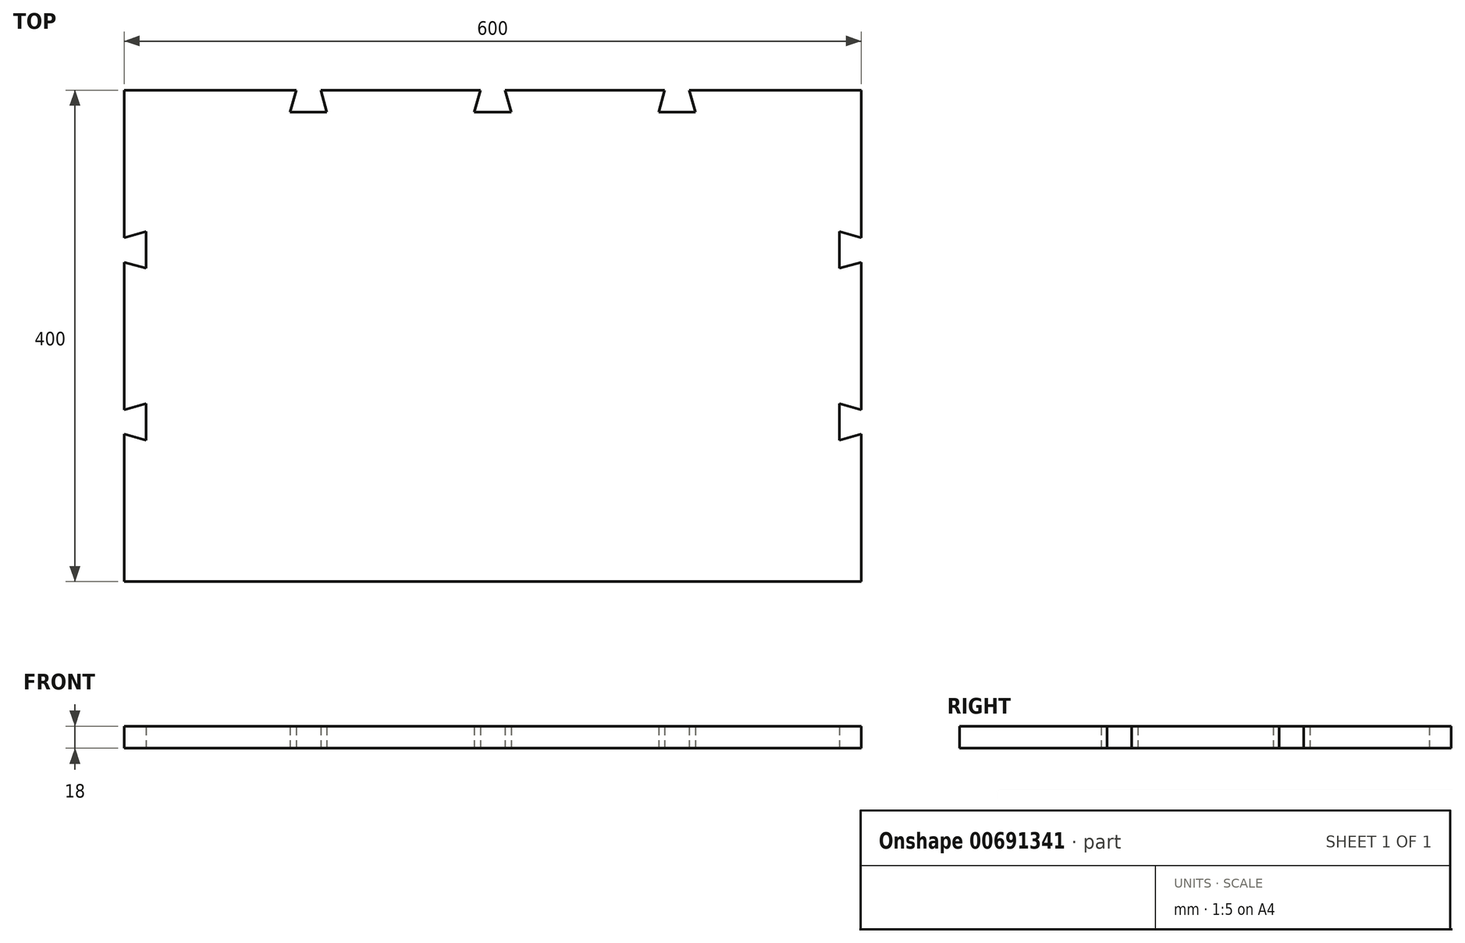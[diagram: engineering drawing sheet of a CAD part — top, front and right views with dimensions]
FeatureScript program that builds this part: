
annotation { "Feature Type Name" : "Feature", "Feature Type Description" : "" }
export const myFeature = defineFeature(function(context is Context, id is Id, definition is map)
    precondition{}
    {
        {
            var Q0;
            Q0=qCreatedBy(makeId("Right.planeOp"),FACE);
            var sketch = newSketch(context, id + "F0", { "sketchPlane" : qUnion([Q0])});
            skLineSegment(sketch, "E0", {"start": v(0, 0) * mm, "end": v(0, 18) * mm});
            skLineSegment(sketch, "E1", {"start": v(0, 18) * mm, "end": v(400, 18) * mm});
            skLineSegment(sketch, "E2", {"start": v(400, 18) * mm, "end": v(400, 0) * mm});
            skLineSegment(sketch, "E3", {"start": v(400, 0) * mm, "end": v(0, 0) * mm});
            skSolve(sketch);
        }
        {
            var Q0;
            Q0=makeQuery(id+"F0.imprint","IMPRINT",FACE,{"disambiguationData":[TD([[makeQuery(id+"F0.imprint","IMPRINT",EDGE,{"derivedFrom":sQuery(id+"F0.wireOp",EDGE,"E0")}),-1.0]])]});
            extrude(context, id + "F1", {"entities" : qUnion([Q0]), "oppositeDirection" : true, "depth" : 600 * mm, "offsetDistance" : 25 * mm});
        }
        {
            var Q0;
            Q0=qCreatedBy(makeId("Top.planeOp"),FACE);
            var sketch = newSketch(context, id + "F2", { "sketchPlane" : qUnion([Q0])});
            skLineSegment(sketch, "E4", {"start": v(-300, -47.28) * mm, "end": v(-300, 479.56) * mm, "construction": true});
            skLineSegment(sketch, "E5", {"start": v(-652.6, 200) * mm, "end": v(61.07, 200) * mm, "construction": true});
            skLineSegment(sketch, "E6", {"start": v(-310, 400) * mm, "end": v(-315, 382) * mm});
            skLineSegment(sketch, "E7", {"start": v(-315, 382) * mm, "end": v(-300, 382) * mm});
            skLineSegment(sketch, "E8", {"start": v(-310, 400) * mm, "end": v(-300, 400) * mm});
            skLineSegment(sketch, "E9.MirrorCS", {"start": v(-290, 400) * mm, "end": v(-285, 382) * mm});
            skLineSegment(sketch, "E10", {"start": v(-300, 382) * mm, "end": v(-285, 382) * mm});
            skLineSegment(sketch, "E11", {"start": v(-300, 400) * mm, "end": v(-290, 400) * mm});
            skLineSegment(sketch, "E12.1.0.0", {"start": v(-160, 400) * mm, "end": v(-165, 382) * mm});
            skLineSegment(sketch, "E12.1.0.1", {"start": v(-160, 400) * mm, "end": v(-150, 400) * mm});
            skLineSegment(sketch, "E12.1.0.2", {"start": v(-150, 400) * mm, "end": v(-140, 400) * mm});
            skLineSegment(sketch, "E12.1.0.3", {"start": v(-140, 400) * mm, "end": v(-135, 382) * mm});
            skLineSegment(sketch, "E13.1.0.0", {"start": v(-460, 400) * mm, "end": v(-465, 382) * mm});
            skLineSegment(sketch, "E13.1.0.1", {"start": v(-460, 400) * mm, "end": v(-450, 400) * mm});
            skLineSegment(sketch, "E13.1.0.2", {"start": v(-450, 400) * mm, "end": v(-440, 400) * mm});
            skLineSegment(sketch, "E13.1.0.3", {"start": v(-440, 400) * mm, "end": v(-435, 382) * mm});
            skLineSegment(sketch, "E14", {"start": v(-135, 382) * mm, "end": v(-165, 382) * mm});
            skLineSegment(sketch, "E15", {"start": v(-435, 382) * mm, "end": v(-465, 382) * mm});
            skLineSegment(sketch, "E16", {"start": v(-600, 260) * mm, "end": v(-600, 270) * mm, "construction": true});
            skLineSegment(sketch, "E17", {"start": v(-600, 270) * mm, "end": v(-582, 270) * mm, "construction": true});
            skLineSegment(sketch, "E18", {"start": v(-600, 270) * mm, "end": v(-600, 280) * mm});
            skLineSegment(sketch, "E19", {"start": v(-600, 280) * mm, "end": v(-582, 285) * mm});
            skLineSegment(sketch, "E20", {"start": v(-582, 285) * mm, "end": v(-582, 270) * mm});
            skLineSegment(sketch, "E21.MirrorCS", {"start": v(-600, 270) * mm, "end": v(-600, 260) * mm});
            skLineSegment(sketch, "E22.MirrorCS", {"start": v(-600, 260) * mm, "end": v(-582, 255) * mm});
            skLineSegment(sketch, "E23.MirrorCS", {"start": v(-582, 255) * mm, "end": v(-582, 270) * mm});
            skLineSegment(sketch, "E24.MirrorCS", {"start": v(-600, 140) * mm, "end": v(-582, 145) * mm});
            skLineSegment(sketch, "E25.MirrorCS", {"start": v(-582, 145) * mm, "end": v(-582, 130) * mm});
            skLineSegment(sketch, "E26.MirrorCS", {"start": v(-582, 115) * mm, "end": v(-582, 130) * mm});
            skLineSegment(sketch, "E27.MirrorCS", {"start": v(-600, 120) * mm, "end": v(-582, 115) * mm});
            skLineSegment(sketch, "E28.MirrorCS", {"start": v(-600, 130) * mm, "end": v(-600, 120) * mm});
            skLineSegment(sketch, "E29.MirrorCS", {"start": v(0, 280) * mm, "end": v(-18, 285) * mm});
            skLineSegment(sketch, "E30.MirrorCS", {"start": v(-18, 285) * mm, "end": v(-18, 270) * mm});
            skLineSegment(sketch, "E31.MirrorCS", {"start": v(0, 270) * mm, "end": v(0, 280) * mm});
            skLineSegment(sketch, "E32.MirrorCS", {"start": v(0, 260) * mm, "end": v(-18, 255) * mm});
            skLineSegment(sketch, "E33.MirrorCS", {"start": v(-18, 255) * mm, "end": v(-18, 270) * mm});
            skLineSegment(sketch, "E34.MirrorCS", {"start": v(0, 270) * mm, "end": v(0, 260) * mm});
            skLineSegment(sketch, "E35.MirrorCS", {"start": v(0, 270) * mm, "end": v(-18, 270) * mm, "construction": true});
            skLineSegment(sketch, "E36.MirrorCS", {"start": v(0, 120) * mm, "end": v(-18, 115) * mm});
            skLineSegment(sketch, "E37.MirrorCS", {"start": v(-18, 145) * mm, "end": v(-18, 130) * mm});
            skLineSegment(sketch, "E38.MirrorCS", {"start": v(-18, 115) * mm, "end": v(-18, 130) * mm});
            skLineSegment(sketch, "E39.MirrorCS", {"start": v(0, 140) * mm, "end": v(-18, 145) * mm});
            skLineSegment(sketch, "E40.MirrorCS", {"start": v(0, 130) * mm, "end": v(0, 120) * mm});
            skLineSegment(sketch, "E41.MirrorCS", {"start": v(0, 260) * mm, "end": v(0, 270) * mm, "construction": true});
            skLineSegment(sketch, "E42", {"start": v(-600, 130) * mm, "end": v(-600, 140) * mm});
            skLineSegment(sketch, "E43", {"start": v(0, 130) * mm, "end": v(0, 140) * mm});
            skPoint(sketch, "E44.orphan", {"position": v(0, 200) * mm});
            skPoint(sketch, "E45.orphan", {"position": v(-600, 200) * mm});
            skSolve(sketch);
        }
        {
            var Q0;
            Q0 = qSketchRegion(id + "F2", true);
            extrude(context, id + "F3", {"entities" : qUnion([Q0]), "operationType" : NewBodyOperationType.REMOVE, "depth" : 18 * mm, "offsetDistance" : 25 * mm, "hasSecondDirection" : true, "secondDirectionOppositeDirection" : true, "secondDirectionDepth" : 25 * mm});
        }
    });
